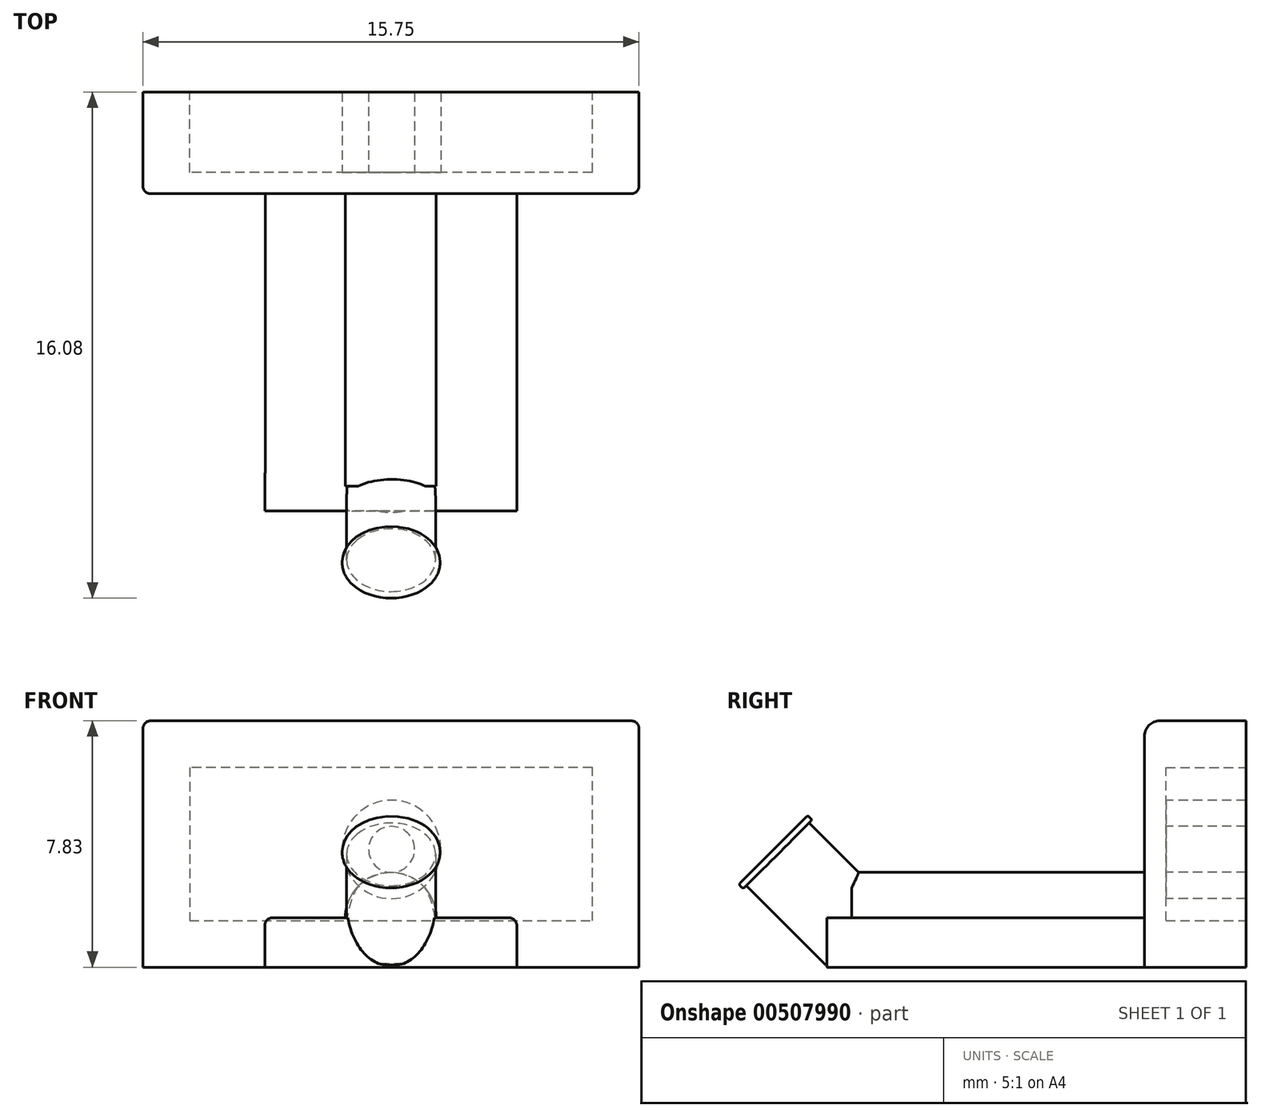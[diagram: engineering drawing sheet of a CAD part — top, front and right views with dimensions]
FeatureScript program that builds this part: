
annotation { "Feature Type Name" : "Feature", "Feature Type Description" : "" }
export const myFeature = defineFeature(function(context is Context, id is Id, definition is map)
    precondition{}
    {
        {
            var Q0;
            Q0=qCreatedBy(makeId("Front.planeOp"),FACE);
            var sketch = newSketch(context, id + "F0", { "sketchPlane" : qUnion([Q0])});
            skLineSegment(sketch, "E0.bottom", {"start": v(-3.4, 1.78) * mm, "end": v(12.35, 1.78) * mm});
            skLineSegment(sketch, "E0.top", {"start": v(-3.4, -6.05) * mm, "end": v(12.35, -6.05) * mm});
            skLineSegment(sketch, "E0.left", {"start": v(-3.4, 1.78) * mm, "end": v(-3.4, -6.05) * mm});
            skLineSegment(sketch, "E0.right", {"start": v(12.35, 1.78) * mm, "end": v(12.35, -6.05) * mm});
            skSolve(sketch);
        }
        {
            var Q0;
            Q0 = qSketchRegion(id + "F0", true);
            extrude(context, id + "F1", {"entities" : qUnion([Q0]), "depth" : 3.23 * mm});
        }
        {
            var Q0;
            Q0=makeQuery(id+"F1.opExtrude","CAP_FACE",FACE,{"disambiguationData":[OSD([sQuery(id+"F0.wireOp",EDGE,"E0.bottom"),sQuery(id+"F0.wireOp",EDGE,"E0.top"),sQuery(id+"F0.wireOp",EDGE,"E0.left"),sQuery(id+"F0.wireOp",EDGE,"E0.right")])],"isStart":false});
            var sketch = newSketch(context, id + "F2", { "sketchPlane" : qUnion([Q0])});
            skPoint(sketch, "E1", {"position": v(8.47, -6.05) * mm});
            skPoint(sketch, "E2", {"position": v(0.48, -6.05) * mm});
            skLineSegment(sketch, "E3", {"start": v(0.48, -6.05) * mm, "end": v(8.47, -6.05) * mm});
            skLineSegment(sketch, "E4", {"start": v(0.48, -6.05) * mm, "end": v(0.48, -4.48) * mm});
            skLineSegment(sketch, "E5", {"start": v(8.47, -6.05) * mm, "end": v(8.47, -4.48) * mm});
            skLineSegment(sketch, "E6", {"start": v(8.47, -4.48) * mm, "end": v(0.48, -4.48) * mm});
            skSolve(sketch);
        }
        {
            var Q0;
            Q0 = qSketchRegion(id + "F2", true);
            extrude(context, id + "F3", {"entities" : qUnion([Q0]), "operationType" : NewBodyOperationType.ADD, "depth" : 9.63 * mm});
        }
        {
            var Q0;
            Q0=makeQuery(id+"F1.opExtrude","CAP_FACE",FACE,{"disambiguationData":[OSD([sQuery(id+"F0.wireOp",EDGE,"E0.bottom"),sQuery(id+"F0.wireOp",EDGE,"E0.top"),sQuery(id+"F0.wireOp",EDGE,"E0.left"),sQuery(id+"F0.wireOp",EDGE,"E0.right")])],"isStart":true});
            var sketch = newSketch(context, id + "F4", { "sketchPlane" : qUnion([Q0])});
            skLineSegment(sketch, "E7", {"start": v(-10.87, 0.3) * mm, "end": v(1.92, 0.3) * mm});
            skLineSegment(sketch, "E8", {"start": v(1.92, 0.3) * mm, "end": v(1.92, -4.57) * mm});
            skLineSegment(sketch, "E9", {"start": v(1.92, -4.57) * mm, "end": v(-10.87, -4.57) * mm});
            skLineSegment(sketch, "E10", {"start": v(-10.87, -4.57) * mm, "end": v(-10.87, 0.3) * mm});
            skSolve(sketch);
        }
        {
            var Q0;
            Q0 = qSketchRegion(id + "F4", true);
            extrude(context, id + "F5", {"entities" : qUnion([Q0]), "operationType" : NewBodyOperationType.REMOVE, "oppositeDirection" : true, "depth" : 2.55 * mm});
        }
        {
            var Q0;
            Q0=makeQuery(id+"F5.boolean.opBoolean","COPY",FACE,{"derivedFrom":makeQuery(id+"F5.opExtrude","CAP_FACE",FACE,{"disambiguationData":[OSD([sQuery(id+"F4.wireOp",EDGE,"E7"),sQuery(id+"F4.wireOp",EDGE,"E8"),sQuery(id+"F4.wireOp",EDGE,"E9"),sQuery(id+"F4.wireOp",EDGE,"E10")])],"isStart":false})});
            var sketch = newSketch(context, id + "F6", { "sketchPlane" : qUnion([Q0])});
            skCircle(sketch, "E11", {"center": v(-4.5, -2.3) * mm, "radius": 1.56 * mm});
            skCircle(sketch, "E12", {"center": v(-4.5, -2.3) * mm, "radius": 0.73 * mm});
            skSolve(sketch);
        }
        {
            var Q0;
            Q0=makeQuery(id+"F6.imprint","IMPRINT",FACE,{"disambiguationData":[TD([[makeQuery(id+"F6.imprint","IMPRINT",EDGE,{"derivedFrom":sQuery(id+"F6.wireOp",EDGE,"E11")}),1.0]])]});
            extrude(context, id + "F7", {"entities" : qUnion([Q0]), "operationType" : NewBodyOperationType.ADD, "depth" : 2.54 * mm});
        }
        {
            var Q0;
            Q0=makeQuery(id+"F3.opExtrude","CAP_EDGE",EDGE,{"disambiguationData":[OSD([sQuery(id+"F2.wireOp",EDGE,"E6")])],"isStart":false});
            chamfer(context, id + "F8", {"entities" : qUnion([Q0]), "width" : 1 * mm, "tangentPropagation" : true});
        }
        {
            var Q0;
            Q0=makeQuery(id+"F8.opChamfer","BLEND_FACE",FACE,{"disambiguationData":[OSD([sQuery(id+"F2.wireOp",EDGE,"E6")])]});
            var sketch = newSketch(context, id + "F9", { "sketchPlane" : qUnion([Q0])});
            skCircle(sketch, "E13", {"center": v(4.48, -12.26) * mm, "radius": 1.41 * mm});
            skSolve(sketch);
        }
        {
            var Q0;
            Q0 = qSketchRegion(id + "F9", true);
            extrude(context, id + "F10", {"entities" : qUnion([Q0]), "operationType" : NewBodyOperationType.ADD, "depth" : 3.76 * mm});
        }
        {
            var Q0;
            Q0=makeQuery(id+"F3.opExtrude","SWEPT_FACE",FACE,{"disambiguationData":[OSD([sQuery(id+"F2.wireOp",EDGE,"E5")])]});
            var sketch = newSketch(context, id + "F11", { "sketchPlane" : qUnion([Q0])});
            skLineSegment(sketch, "E14", {"start": v(-12.86, -6.05) * mm, "end": v(-15.16, -6.05) * mm});
            skLineSegment(sketch, "E15", {"start": v(-15.16, -6.05) * mm, "end": v(-13.45, -8.64) * mm});
            skLineSegment(sketch, "E16", {"start": v(-13.45, -8.64) * mm, "end": v(-12.86, -6.05) * mm});
            skSolve(sketch);
        }
        {
            var Q0;
            Q0 = qSketchRegion(id + "F11", true);
            extrude(context, id + "F12", {"entities" : qUnion([Q0]), "operationType" : NewBodyOperationType.REMOVE, "oppositeDirection" : true, "depth" : 25 * mm});
        }
        {
            var Q0;
            Q0=makeQuery(id+"F3.opExtrude","SWEPT_FACE",FACE,{"disambiguationData":[OSD([sQuery(id+"F2.wireOp",EDGE,"E5")])]});
            var sketch = newSketch(context, id + "F13", { "sketchPlane" : qUnion([Q0])});
            skLineSegment(sketch, "E17", {"start": v(-12.86, -6.05) * mm, "end": v(-13.31, -6.05) * mm});
            skLineSegment(sketch, "E18", {"start": v(-13.31, -6.05) * mm, "end": v(-13.31, -4.48) * mm});
            skLineSegment(sketch, "E19", {"start": v(-13.31, -4.48) * mm, "end": v(-11.86, -4.48) * mm});
            skLineSegment(sketch, "E20", {"start": v(-11.86, -4.48) * mm, "end": v(-12.86, -5.48) * mm});
            skLineSegment(sketch, "E21", {"start": v(-12.86, -5.48) * mm, "end": v(-12.86, -6.05) * mm});
            skSolve(sketch);
        }
        {
            var Q0;
            Q0 = qSketchRegion(id + "F13", true);
            extrude(context, id + "F14", {"entities" : qUnion([Q0]), "operationType" : NewBodyOperationType.ADD, "oppositeDirection" : true, "depth" : 8 * mm});
        }
        {
            var Q0;
            Q0=makeQuery(id+"F10.opExtrude","CAP_FACE",FACE,{"disambiguationData":[OSD([sQuery(id+"F9.wireOp",EDGE,"E13")])],"isStart":false});
            var sketch = newSketch(context, id + "F15", { "sketchPlane" : qUnion([Q0])});
            skCircle(sketch, "E22", {"center": v(4.48, -12.26) * mm, "radius": 1.55 * mm});
            skSolve(sketch);
        }
        {
            var Q0;
            Q0 = qSketchRegion(id + "F15", true);
            extrude(context, id + "F16", {"entities" : qUnion([Q0]), "operationType" : NewBodyOperationType.ADD, "oppositeDirection" : true, "depth" : 0.2 * mm});
        }
        {
            var Q0;
            Q0=makeQuery(id+"F16.opExtrude","CAP_EDGE",EDGE,{"disambiguationData":[OSD([sQuery(id+"F15.wireOp",EDGE,"E22")])],"isStart":false});
            fillet(context, id + "F17", {"entities" : qUnion([Q0]), "radius" : 0.07 * mm, "tangentPropagation" : true, "allowEdgeOverflow" : false});
        }
        {
            var Q0;
            Q0=makeQuery(id+"F16.opExtrude","CAP_EDGE",EDGE,{"disambiguationData":[OSD([sQuery(id+"F15.wireOp",EDGE,"E22")])],"isStart":true});
            fillet(context, id + "F18", {"entities" : qUnion([Q0]), "radius" : 0.07 * mm, "tangentPropagation" : true, "allowEdgeOverflow" : false});
        }
        {
            var Q0;
            Q0=makeQuery(id+"F14.boolean.opBoolean","MERGE",EDGE,{"derivedFrom":[makeQuery(id+"F3.opExtrude","SWEPT_EDGE",EDGE,{"disambiguationData":[OSD([sQuery(id+"F2.wireOp",EDGE,"E5"),sQuery(id+"F2.wireOp",EDGE,"E6")])]}),makeQuery(id+"F14.opExtrude","CAP_EDGE",EDGE,{"disambiguationData":[OSD([sQuery(id+"F13.wireOp",EDGE,"E19")])],"isStart":true})]});
            fillet(context, id + "F19", {"entities" : qUnion([Q0]), "radius" : 0.24 * mm, "tangentPropagation" : true, "allowEdgeOverflow" : false});
        }
        {
            var Q0;
            Q0=makeQuery(id+"F14.opExtrude","CAP_EDGE",EDGE,{"disambiguationData":[OSD([sQuery(id+"F13.wireOp",EDGE,"E19")])],"isStart":false});
            fillet(context, id + "F20", {"entities" : qUnion([Q0]), "radius" : 0.24 * mm, "tangentPropagation" : true, "allowEdgeOverflow" : false});
        }
        {
            var Q0;
            Q0=makeQuery(id+"F1.opExtrude","CAP_EDGE",EDGE,{"disambiguationData":[OSD([sQuery(id+"F0.wireOp",EDGE,"E0.bottom")])],"isStart":false});
            fillet(context, id + "F21", {"entities" : qUnion([Q0]), "radius" : 0.48 * mm, "tangentPropagation" : true, "allowEdgeOverflow" : false});
        }
        {
            var Q0;
            Q0=makeQuery(id+"F1.opExtrude","CAP_EDGE",EDGE,{"disambiguationData":[OSD([sQuery(id+"F0.wireOp",EDGE,"E0.left")])],"isStart":false});
            fillet(context, id + "F22", {"entities" : qUnion([Q0]), "radius" : 0.24 * mm, "tangentPropagation" : true, "allowEdgeOverflow" : false});
        }
        {
            var Q0;
            Q0=makeQuery(id+"F1.opExtrude","CAP_EDGE",EDGE,{"disambiguationData":[OSD([sQuery(id+"F0.wireOp",EDGE,"E0.right")])],"isStart":false});
            fillet(context, id + "F23", {"entities" : qUnion([Q0]), "radius" : 0.24 * mm, "tangentPropagation" : true, "allowEdgeOverflow" : false});
        }
        {
            var Q0;
            Q0=makeQuery(id+"F1.opExtrude","CAP_FACE",FACE,{"disambiguationData":[OSD([sQuery(id+"F0.wireOp",EDGE,"E0.bottom"),sQuery(id+"F0.wireOp",EDGE,"E0.top"),sQuery(id+"F0.wireOp",EDGE,"E0.left"),sQuery(id+"F0.wireOp",EDGE,"E0.right")])],"isStart":false});
            var sketch = newSketch(context, id + "F24", { "sketchPlane" : qUnion([Q0])});
            skCircle(sketch, "E23", {"center": v(4.47, -4.48) * mm, "radius": 1.45 * mm});
            skSolve(sketch);
        }
        {
            var Q0;
            Q0 = qSketchRegion(id + "F24", true);
            extrude(context, id + "F25", {"entities" : qUnion([Q0]), "operationType" : NewBodyOperationType.ADD, "depth" : 9.3 * mm});
        }
    });
